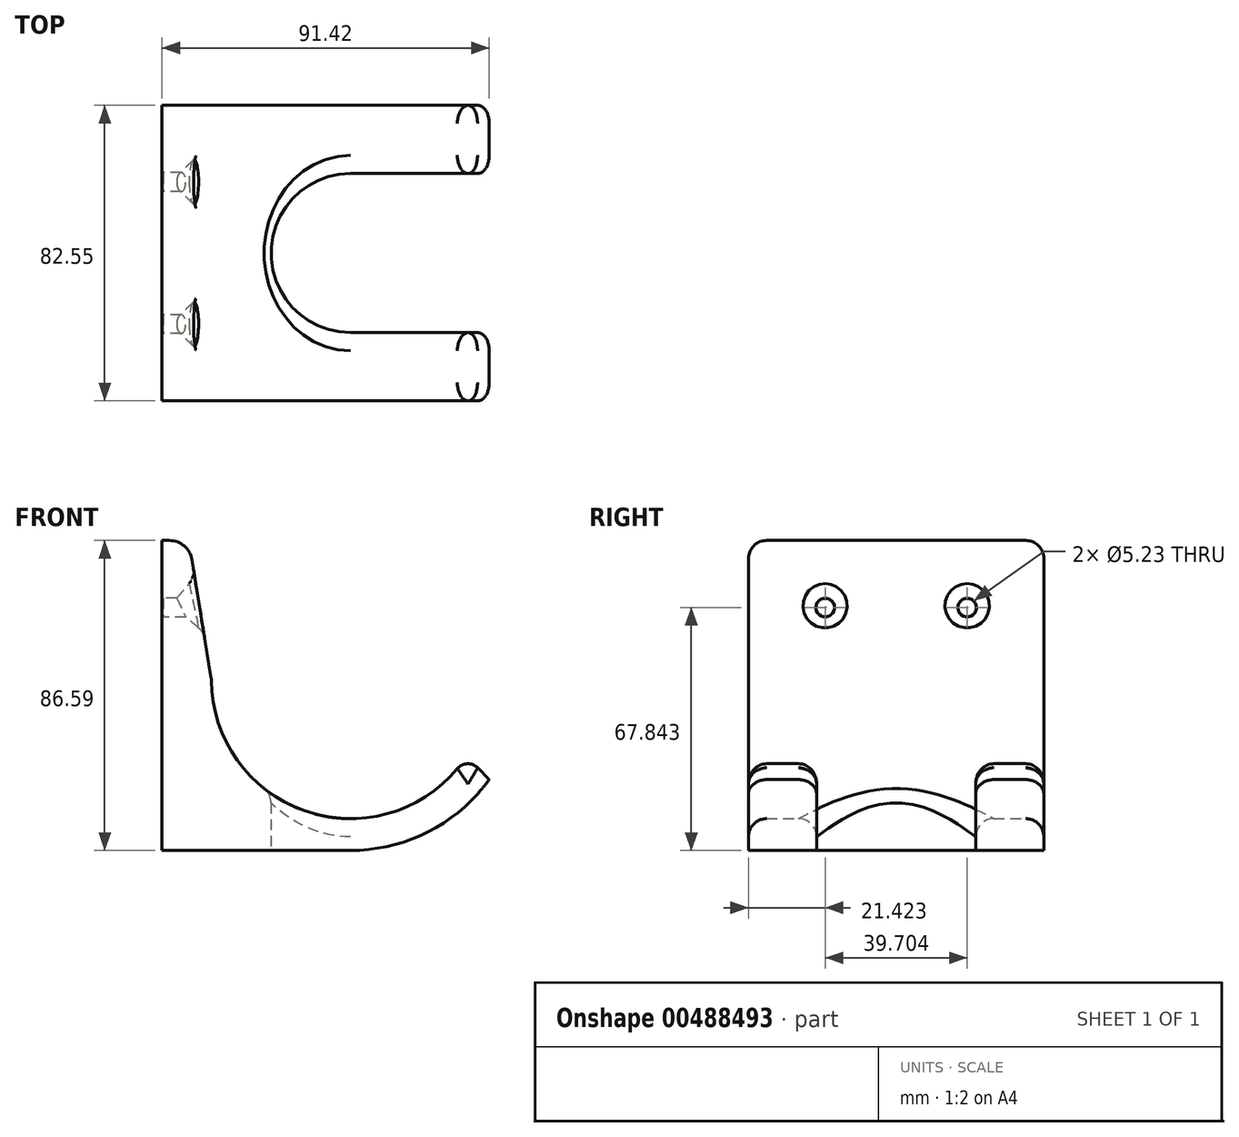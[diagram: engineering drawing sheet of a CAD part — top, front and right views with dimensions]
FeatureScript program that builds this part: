
annotation { "Feature Type Name" : "Feature", "Feature Type Description" : "" }
export const myFeature = defineFeature(function(context is Context, id is Id, definition is map)
    precondition{}
    {
        {
            var Q0;
            Q0=qCreatedBy(makeId("Front.planeOp"),FACE);
            var sketch = newSketch(context, id + "F0", { "sketchPlane" : qUnion([Q0])});
            skArc(sketch, "E0", {"start": v(-38.9, 0) * mm, "mid": v(-13.26, -36.57) * mm, "end": v(29.86, -24.92) * mm});
            skPoint(sketch, "E1", {"position": v(-38.9, 0) * mm});
            skPoint(sketch, "E2", {"position": v(38.9, 0) * mm});
            skArc(sketch, "E3.0", {"start": v(-47.78, 0) * mm, "mid": v(-14.7, -45.46) * mm, "end": v(38.73, -27.98) * mm});
            skLineSegment(sketch, "E4", {"start": v(-38.9, 0) * mm, "end": v(-47.78, 0) * mm});
            skLineSegment(sketch, "E5.bottom", {"start": v(-47.78, 0) * mm, "end": v(-52.69, 0) * mm});
            skLineSegment(sketch, "E5.top", {"start": v(-50.64, 38.8) * mm, "end": v(-52.69, 38.8) * mm});
            skLineSegment(sketch, "E5.right", {"start": v(-52.69, 0) * mm, "end": v(-52.69, 38.8) * mm});
            skLineSegment(sketch, "E6", {"start": v(-44.37, 33.48) * mm, "end": v(-38.9, 0) * mm});
            skLineSegment(sketch, "E7", {"start": v(-52.69, 0) * mm, "end": v(-52.69, -47.78) * mm});
            skLineSegment(sketch, "E8", {"start": v(-52.69, -47.78) * mm, "end": v(0, -47.78) * mm});
            skPoint(sketch, "E9.visualSharp", {"position": v(-45.24, 38.8) * mm});
            skArc(sketch, "E9.filletArc", {"start": v(-44.37, 33.48) * mm, "mid": v(-46.53, 37.3) * mm, "end": v(-50.64, 38.8) * mm});
            skPoint(sketch, "E10.visualSharp", {"position": v(47.78, 0) * mm});
            skLineSegment(sketch, "E11", {"start": v(38.73, -27.98) * mm, "end": v(38.73, -47.94) * mm});
            skLineSegment(sketch, "E12", {"start": v(38.73, -47.94) * mm, "end": v(0, -47.78) * mm});
            skLineSegment(sketch, "E13", {"start": v(35.5, -24.7) * mm, "end": v(38.73, -27.98) * mm});
            skPoint(sketch, "E14.visualSharp", {"position": v(32.4, -21.53) * mm});
            skArc(sketch, "E14.filletArc", {"start": v(35.5, -24.7) * mm, "mid": v(32.63, -23.56) * mm, "end": v(29.86, -24.92) * mm});
            skSolve(sketch);
        }
        {
            var Q0;
            {var subQ0=sQuery(id+"F0.wireOp",EDGE,"E5.bottom");Q0=makeQuery(id+"F0.imprint","IMPRINT",FACE,{"disambiguationData":[TD([[makeQuery(id+"F0.imprint","IMPRINT",EDGE,{"derivedFrom":subQ0}),1.0]])]});}
            var Q1;
            Q1=makeQuery(id+"F0.imprint","IMPRINT",FACE,{"disambiguationData":[TD([[makeQuery(id+"F0.imprint","IMPRINT",EDGE,{"derivedFrom":sQuery(id+"F0.wireOp",EDGE,"E4")}),-1.0]])]});
            var Q2;
            Q2=makeQuery(id+"F0.imprint","IMPRINT",FACE,{"disambiguationData":[TD([[makeQuery(id+"F0.imprint","IMPRINT",EDGE,{"derivedFrom":sQuery(id+"F0.wireOp",EDGE,"E0")}),-1.0]])]});
            extrude(context, id + "F1", {"entities" : qUnion([Q0, Q1, Q2]), "depth" : 82.55 * mm});
        }
        {
            var Q0;
            Q0=makeQuery(id+"F1.opExtrude","SWEPT_FACE",FACE,{"disambiguationData":[OSD([sQuery(id+"F0.wireOp",EDGE,"E8")])]});
            var sketch = newSketch(context, id + "F2", { "sketchPlane" : qUnion([Q0])});
            skCircle(sketch, "E15", {"center": v(0, 41.28) * mm, "radius": 22.23 * mm});
            skLineSegment(sketch, "E16.bottom", {"start": v(0, 63.5) * mm, "end": v(53.65, 63.5) * mm});
            skLineSegment(sketch, "E16.top", {"start": v(0, 19.05) * mm, "end": v(53.65, 19.05) * mm});
            skLineSegment(sketch, "E16.left", {"start": v(0, 63.5) * mm, "end": v(0, 19.05) * mm});
            skLineSegment(sketch, "E16.right", {"start": v(53.65, 63.5) * mm, "end": v(53.65, 19.05) * mm});
            skSolve(sketch);
        }
        {
            var Q0;
            Q0 = qSketchRegion(id + "F2", true);
            extrude(context, id + "F3", {"entities" : qUnion([Q0]), "operationType" : NewBodyOperationType.REMOVE, "oppositeDirection" : true, "depth" : 76.2 * mm});
        }
        {
            var Q0;
            Q0=makeQuery(id+"F1.opExtrude","SWEPT_FACE",FACE,{"disambiguationData":[OSD([sQuery(id+"F0.wireOp",EDGE,"E5.right"),sQuery(id+"F0.wireOp",EDGE,"E7")])]});
            var sketch = newSketch(context, id + "F4", { "sketchPlane" : qUnion([Q0])});
            skCircle(sketch, "E17", {"center": v(21.42, 20.06) * mm, "radius": 2.61 * mm});
            skLineSegment(sketch, "E18", {"start": v(41.28, 38.8) * mm, "end": v(41.28, 6.96) * mm});
            skPoint(sketch, "E18.endSnap0", {"position": v(41.28, 38.8) * mm});
            skCircle(sketch, "E19.MirrorC", {"center": v(61.13, 20.06) * mm, "radius": 2.61 * mm});
            skSolve(sketch);
        }
        {
            var Q0;
            Q0 = qSketchRegion(id + "F4", true);
            extrude(context, id + "F5", {"entities" : qUnion([Q0]), "operationType" : NewBodyOperationType.REMOVE, "oppositeDirection" : true, "depth" : 25.4 * mm});
        }
        {
            var Q0;
            Q0=makeQuery(id+"F5.boolean.opBoolean","INTERSECT",EDGE,{"derivedFrom":[makeQuery(id+"F1.opExtrude","SWEPT_FACE",FACE,{"disambiguationData":[OSD([sQuery(id+"F0.wireOp",EDGE,"E6")])]}),makeQuery(id+"F5.opExtrude","SWEPT_FACE",FACE,{"disambiguationData":[OSD([sQuery(id+"F4.wireOp",EDGE,"E19.MirrorC")])]})]});
            var Q1;
            Q1=makeQuery(id+"F5.boolean.opBoolean","INTERSECT",EDGE,{"derivedFrom":[makeQuery(id+"F1.opExtrude","SWEPT_FACE",FACE,{"disambiguationData":[OSD([sQuery(id+"F0.wireOp",EDGE,"E6")])]}),makeQuery(id+"F5.opExtrude","SWEPT_FACE",FACE,{"disambiguationData":[OSD([sQuery(id+"F4.wireOp",EDGE,"E17")])]})]});
            chamfer(context, id + "F6", {"entities" : qUnion([Q0, Q1]), "width" : 5.08 * mm, "tangentPropagation" : true});
        }
        {
            var Q0;
            Q0=makeQuery(id+"F1.opExtrude","SWEPT_FACE",FACE,{"disambiguationData":[OSD([sQuery(id+"F0.wireOp",EDGE,"E5.right"),sQuery(id+"F0.wireOp",EDGE,"E7")])]});
            var sketch = newSketch(context, id + "F7", { "sketchPlane" : qUnion([Q0])});
            skCircle(sketch, "E20", {"center": v(21.42, 20.06) * mm, "radius": 2.57 * mm});
            skCircle(sketch, "E21", {"center": v(61.13, 20.06) * mm, "radius": 2.6 * mm});
            skSolve(sketch);
        }
        {
            var Q0;
            Q0 = qSketchRegion(id + "F7", true);
            extrude(context, id + "F8", {"entities" : qUnion([Q0]), "oppositeDirection" : true, "depth" : .3 * mm});
        }
        {
            var Q0;
            Q0=makeQuery(id+"F1.opExtrude","CAP_EDGE",EDGE,{"disambiguationData":[OSD([sQuery(id+"F0.wireOp",EDGE,"E0")])],"isStart":false});
            var Q1;
            Q1=makeQuery(id+"F1.opExtrude","CAP_EDGE",EDGE,{"disambiguationData":[OSD([sQuery(id+"F0.wireOp",EDGE,"E6")])],"isStart":false});
            var Q2;
            Q2=makeQuery(id+"F3.boolean.opBoolean","INTERSECT",EDGE,{"derivedFrom":[makeQuery(id+"F1.opExtrude","SWEPT_FACE",FACE,{"disambiguationData":[OSD([sQuery(id+"F0.wireOp",EDGE,"E0")])]}),makeQuery(id+"F3.opExtrude","SWEPT_FACE",FACE,{"disambiguationData":[OSD([sQuery(id+"F2.wireOp",EDGE,"E15")])]})]});
            var Q3;
            Q3=makeQuery(id+"F1.opExtrude","CAP_EDGE",EDGE,{"disambiguationData":[OSD([sQuery(id+"F0.wireOp",EDGE,"E0")])],"isStart":true});
            var Q4;
            Q4=makeQuery(id+"F1.opExtrude","SWEPT_FACE",FACE,{"disambiguationData":[OSD([sQuery(id+"F0.wireOp",EDGE,"E6")])]});
            fillet(context, id + "F9", {"entities" : qUnion([Q0, Q1, Q2, Q3, Q4]), "radius" : 5.08 * mm, "tangentPropagation" : true, "allowEdgeOverflow" : false});
        }
    });
